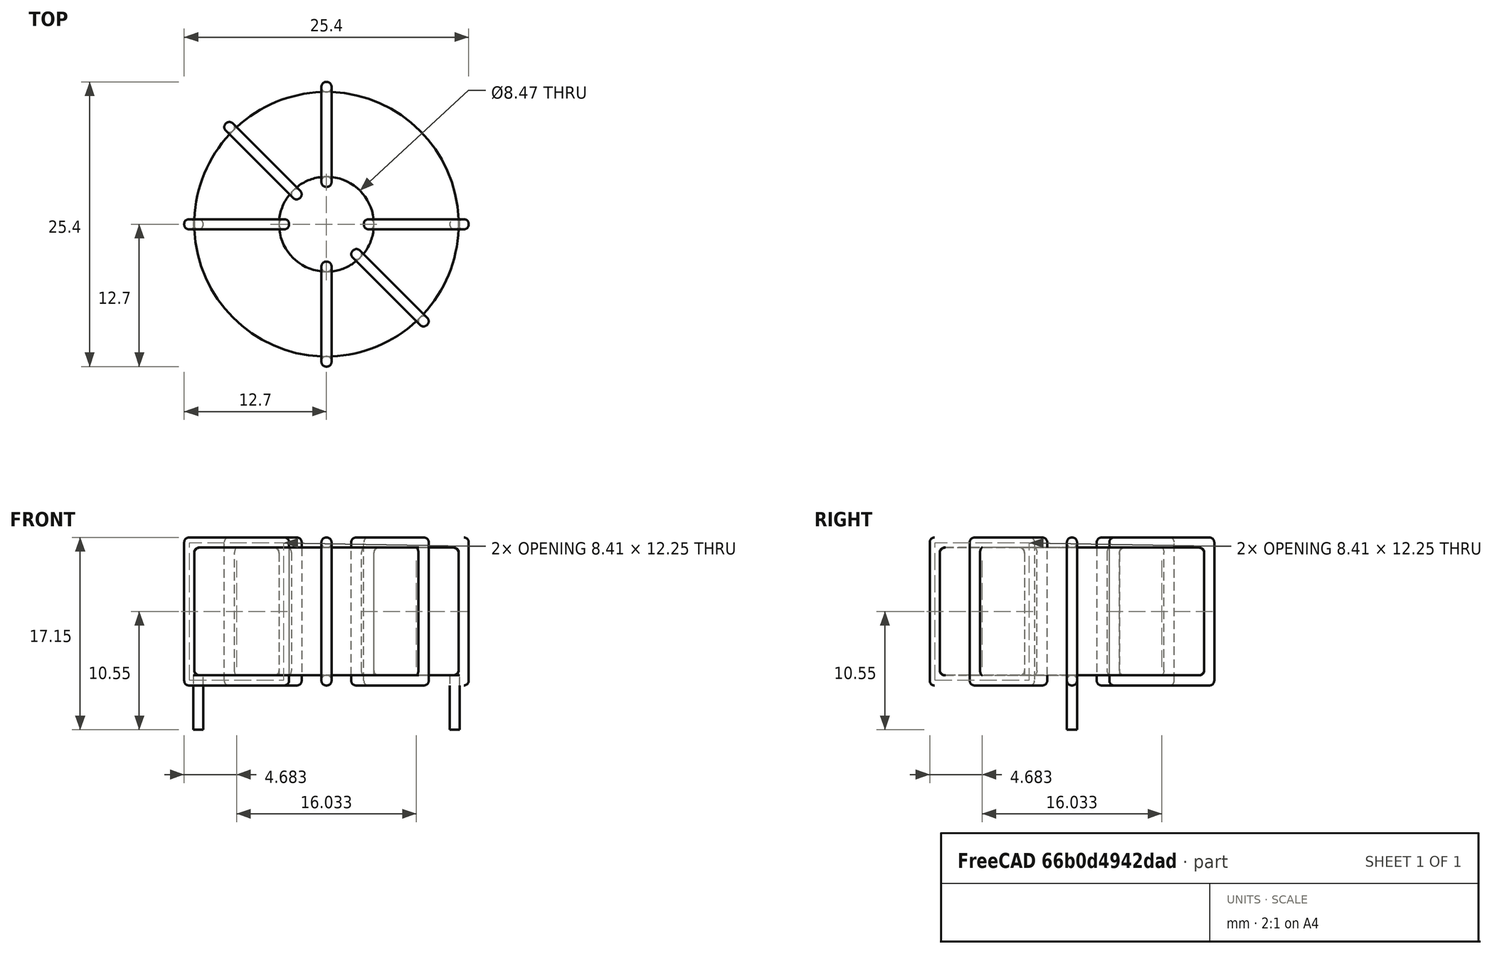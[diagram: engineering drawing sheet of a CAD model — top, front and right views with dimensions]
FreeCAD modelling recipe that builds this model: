
FCSTD DOCUMENT  (FreeCAD 0.16R6703 (Git))
Label: L_Toroid_Horizontal_D25.4mm_P22.90mm_Vishay_TJ5
License: All rights reserved
LicenseURL: http://en.wikipedia.org/wiki/All_rights_reserved
objects: Sketcher::SketchObject×6, PartDesign::Pad×6, PartDesign::Fillet×5, Spreadsheet::Sheet×1
note: 23 computed .brp shape members not serialized (recipe doc carries the construction recipe); baked Part::Feature solids carry a one-line shape summary decoded from their .brp

FEATURE [Spreadsheet::Sheet] Spreadsheet  label="dimensions"
  cells = A1=Wx; B1(Wx)=25.4; C1(WW)=8.466666666666667; D1=25.4; A2=Wy; B2(Wy)=25.4; D2=25.4; A3=RM; B3(RMx)=22.9; C3(RMy)=0; A4=d_wire; B4(d_wire)=0.8999999999999999; A5=H; B5(H)=11.4; A6=offsetx; B6(offsetx)=1.25
FEATURE [Sketcher::SketchObject] Sketch
  Placement = pos=(0,0,1.4) rot=(0,0,1;0rad)
  expr: Placement.Base.z = 0.5 + Spreadsheet.d_wire
  expr: Constraints[0] = Spreadsheet.Wx / 2 - Spreadsheet.d_wire
  expr: Constraints[4] = Spreadsheet.WW / 2
  expr: Constraints[2] = Spreadsheet.RMy / 2
  expr: Constraints[1] = Spreadsheet.RMx / 2
  sketch-geometry (2):
    g0: Circle CenterX=11.45 CenterY=0 CenterZ=0 NormalX=0 NormalY=0 NormalZ=1 Radius=11.8
    g1: Circle CenterX=11.45 CenterY=0 CenterZ=0 NormalX=0 NormalY=0 NormalZ=1 Radius=4.23333
  constraints (5):
    c: Radius(g0) = 11.8
    c: DistanceX(g-1,g0) = 11.45
    c: DistanceY(g-1,g0) = 0
    c: Coincident(g1,g0)
    c: Radius(g1) = 4.23333
FEATURE [PartDesign::Pad] Pad
  Length = 11.4
  Length2 = 100
  Placement = pos=(0,0,1.4) rot=(0,0,1;0rad)
  Sketch = -> Sketch
  Type = 0
  expr: Length = Spreadsheet.H
FEATURE [Sketcher::SketchObject] Sketch001
  Placement = pos=(0,0,0.95) rot=(0,0,1;0rad)
  expr: Placement.Base.z = 0.5 + Spreadsheet.d_wire * 0.5
  expr: Constraints[4] = Spreadsheet.RMx
  expr: Constraints[2] = Spreadsheet.RMy
  expr: Constraints[1] = Spreadsheet.d_wire / 2
  sketch-geometry (2):
    g0: Circle CenterX=0 CenterY=0 CenterZ=0 NormalX=0 NormalY=0 NormalZ=1 Radius=0.45
    g1: Circle CenterX=22.9 CenterY=0 CenterZ=0 NormalX=0 NormalY=0 NormalZ=1 Radius=0.45
  constraints (5):
    c: Equal(g0,g1)
    c: Radius(g0) = 0.45
    c: DistanceY(g-1,g1) = 0
    c: Coincident(g0,g-1)
    c: DistanceX(g-1,g1) = 22.9
FEATURE [PartDesign::Pad] Pad001
  Length = 0.45
  Length2 = 4.4
  Placement = pos=(0,0,0.95) rot=(0,0,1;0rad)
  Reversed = true
  Sketch = -> Sketch001
  Type = 4
  expr: Length2 = 3.5 + Spreadsheet.d_wire
  expr: Length = Spreadsheet.d_wire / 2
FEATURE [PartDesign::Fillet] Fillet
  Base = -> Pad [Edge6,Edge3,Edge2]
  Placement = pos=(0,0,1.4) rot=(0,0,1;0rad)
  Radius = 0.5
FEATURE [Sketcher::SketchObject] Sketch003
  Placement = pos=(11.45,0,0) rot=(1,0,0;1.5708rad)
  expr: Placement.Base.x = Spreadsheet.RMx / 2
  expr: Constraints[49] = Spreadsheet.Wx - Spreadsheet.d_wire * 2
  expr: Constraints[44] = Spreadsheet.d_wire
  expr: Constraints[23] = Spreadsheet.H
  expr: Constraints[22] = Spreadsheet.Wx / 2 - Spreadsheet.d_wire
  expr: Placement.Base.y = Spreadsheet.RMy / 2
  expr: Constraints[21] = (Spreadsheet.Wx - Spreadsheet.WW) / 2 - Spreadsheet.d_wire
  expr: Constraints[19] = Spreadsheet.d_wire
  expr: Constraints[17] = Spreadsheet.d_wire
  expr: Constraints[18] = Spreadsheet.d_wire
  expr: Constraints[16] = Spreadsheet.d_wire
  sketch-geometry (16):
    g0: LineSegment StartX=-3.33333 StartY=0.5 StartZ=0 EndX=-12.7 EndY=0.5 EndZ=0
    g1: LineSegment StartX=-12.7 StartY=0.5 StartZ=0 EndX=-12.7 EndY=13.7 EndZ=0
    g2: LineSegment StartX=-12.7 StartY=13.7 StartZ=0 EndX=-3.33333 EndY=13.7 EndZ=0
    g3: LineSegment StartX=-3.33333 StartY=13.7 StartZ=0 EndX=-3.33333 EndY=0.5 EndZ=0
    g4: LineSegment StartX=-11.8 StartY=12.8 StartZ=0 EndX=-4.23333 EndY=12.8 EndZ=0
    g5: LineSegment StartX=-4.23333 StartY=12.8 StartZ=0 EndX=-4.23333 EndY=1.4 EndZ=0
    g6: LineSegment StartX=-4.23333 StartY=1.4 StartZ=0 EndX=-11.8 EndY=1.4 EndZ=0
    g7: LineSegment StartX=-11.8 StartY=1.4 StartZ=0 EndX=-11.8 EndY=12.8 EndZ=0
    g8: LineSegment StartX=3.33333 StartY=13.7 StartZ=0 EndX=12.7 EndY=13.7 EndZ=0
    g9: LineSegment StartX=12.7 StartY=13.7 StartZ=0 EndX=12.7 EndY=0.5 EndZ=0
    g10: LineSegment StartX=12.7 StartY=0.5 StartZ=0 EndX=3.33333 EndY=0.5 EndZ=0
    g11: LineSegment StartX=3.33333 StartY=0.5 StartZ=0 EndX=3.33333 EndY=13.7 EndZ=0
    g12: LineSegment StartX=4.23333 StartY=12.8 StartZ=0 EndX=11.8 EndY=12.8 EndZ=0
    g13: LineSegment StartX=11.8 StartY=12.8 StartZ=0 EndX=11.8 EndY=1.4 EndZ=0
    g14: LineSegment StartX=11.8 StartY=1.4 StartZ=0 EndX=4.23333 EndY=1.4 EndZ=0
    g15: LineSegment StartX=4.23333 StartY=1.4 StartZ=0 EndX=4.23333 EndY=12.8 EndZ=0
  constraints (50):
    c: Horizontal(g0)
    c: Coincident(g1,g0)
    c: Vertical(g1)
    c: Coincident(g2,g1)
    c: Horizontal(g2)
    c: Coincident(g3,g2)
    c: Coincident(g3,g0)
    c: Vertical(g3)
    c: Coincident(g4,g5)
    c: Coincident(g5,g6)
    c: Coincident(g6,g7)
    c: Coincident(g7,g4)
    c: Horizontal(g4)
    c: Horizontal(g6)
    c: Vertical(g5)
    c: Vertical(g7)
    c: DistanceX(g1,g4) = 0.9
    c: DistanceY(g4,g1) = 0.9
    c: DistanceX(g5,g0) = 0.9
    c: DistanceY(g0,g5) = 0.9
    c: DistanceY(g-1,g0) = 0.5
    c: DistanceX(g6,g6) = 7.56667
    c: DistanceX(g6,g-1) = 11.8
    c: DistanceY(g7,g7) = 11.4
    c: Coincident(g8,g9)
    c: Coincident(g9,g10)
    c: Coincident(g10,g11)
    c: Coincident(g11,g8)
    c: Horizontal(g8)
    c: Horizontal(g10)
    c: Vertical(g9)
    c: Vertical(g11)
    c: Coincident(g12,g13)
    c: Coincident(g13,g14)
    c: Coincident(g14,g15)
    c: Coincident(g15,g12)
    c: Horizontal(g12)
    c: Horizontal(g14)
    c: Vertical(g13)
    c: Vertical(g15)
    c: DistanceY(g8,g2) = 0
    c: DistanceY(g10,g0) = 0
    c: DistanceY(g14,g5) = 0
    c: DistanceY(g12,g4) = 0
    c: DistanceX(g8,g12) = 0.9
    c: Equal(g8,g2)
    c: Equal(g12,g4)
    c: Equal(g9,g1)
    c: Equal(g13,g7)
    c: DistanceX(g4,g12) = 23.6
FEATURE [PartDesign::Pad] Pad002
  Length = 0.9
  Length2 = 100
  Midplane = true
  Placement = pos=(11.45,0,0) rot=(1,0,0;1.5708rad)
  Sketch = -> Sketch003
  Type = 0
  expr: Length = Spreadsheet.d_wire
FEATURE [PartDesign::Fillet] Fillet001
  Base = -> Pad002 [Edge38,Edge41,Edge42,Edge43,Edge29,Edge32,Edge33,Edge34,Edge25,Edge35,Edge36,Edge13,Edge14,Edge15,Edge16,Edge17,Edge18,Edge19,Edge1,Edge2,Edge3,Edge4,Edge5,Edge6,Edge7,Edge37,Edge39,Edge40,Edge20,Edge23,Edge24,Edge21,Edge22,Edge8,Edge9,Edge10,Edge11,Edge12,Edge26,Edge27,+8 more]
  Placement = pos=(11.45,0,0) rot=(1,0,0;1.5708rad)
  Radius = 0.423
  expr: Radius = Spreadsheet.d_wire * 0.47
FEATURE [Sketcher::SketchObject] Sketch004
  Placement = pos=(11.45,0,0) rot=(0.862856,0.357407,0.357407;1.71777rad)
  expr: Placement.Base.x = Spreadsheet.RMx / 2
  expr: Constraints[49] = Spreadsheet.Wx - 2 * Spreadsheet.d_wire
  expr: Constraints[44] = Spreadsheet.d_wire
  expr: Constraints[23] = Spreadsheet.H
  expr: Constraints[22] = Spreadsheet.Wx / 2 - Spreadsheet.d_wire
  expr: Placement.Base.y = Spreadsheet.RMy / 2
  expr: Constraints[21] = (Spreadsheet.Wx - Spreadsheet.WW) / 2 - Spreadsheet.d_wire
  expr: Constraints[19] = Spreadsheet.d_wire
  expr: Constraints[17] = Spreadsheet.d_wire
  expr: Constraints[18] = Spreadsheet.d_wire
  expr: Constraints[16] = Spreadsheet.d_wire
  sketch-geometry (16):
    g0: LineSegment StartX=-3.33333 StartY=0.5 StartZ=0 EndX=-12.7 EndY=0.5 EndZ=0
    g1: LineSegment StartX=-12.7 StartY=0.5 StartZ=0 EndX=-12.7 EndY=13.7 EndZ=0
    g2: LineSegment StartX=-12.7 StartY=13.7 StartZ=0 EndX=-3.33333 EndY=13.7 EndZ=0
    g3: LineSegment StartX=-3.33333 StartY=13.7 StartZ=0 EndX=-3.33333 EndY=0.5 EndZ=0
    g4: LineSegment StartX=-11.8 StartY=12.8 StartZ=0 EndX=-4.23333 EndY=12.8 EndZ=0
    g5: LineSegment StartX=-4.23333 StartY=12.8 StartZ=0 EndX=-4.23333 EndY=1.4 EndZ=0
    g6: LineSegment StartX=-4.23333 StartY=1.4 StartZ=0 EndX=-11.8 EndY=1.4 EndZ=0
    g7: LineSegment StartX=-11.8 StartY=1.4 StartZ=0 EndX=-11.8 EndY=12.8 EndZ=0
    g8: LineSegment StartX=3.33333 StartY=13.7 StartZ=0 EndX=12.7 EndY=13.7 EndZ=0
    g9: LineSegment StartX=12.7 StartY=13.7 StartZ=0 EndX=12.7 EndY=0.5 EndZ=0
    g10: LineSegment StartX=12.7 StartY=0.5 StartZ=0 EndX=3.33333 EndY=0.5 EndZ=0
    g11: LineSegment StartX=3.33333 StartY=0.5 StartZ=0 EndX=3.33333 EndY=13.7 EndZ=0
    g12: LineSegment StartX=4.23333 StartY=12.8 StartZ=0 EndX=11.8 EndY=12.8 EndZ=0
    g13: LineSegment StartX=11.8 StartY=12.8 StartZ=0 EndX=11.8 EndY=1.4 EndZ=0
    g14: LineSegment StartX=11.8 StartY=1.4 StartZ=0 EndX=4.23333 EndY=1.4 EndZ=0
    g15: LineSegment StartX=4.23333 StartY=1.4 StartZ=0 EndX=4.23333 EndY=12.8 EndZ=0
  constraints (50):
    c: Horizontal(g0)
    c: Coincident(g1,g0)
    c: Vertical(g1)
    c: Coincident(g2,g1)
    c: Horizontal(g2)
    c: Coincident(g3,g2)
    c: Coincident(g3,g0)
    c: Vertical(g3)
    c: Coincident(g4,g5)
    c: Coincident(g5,g6)
    c: Coincident(g6,g7)
    c: Coincident(g7,g4)
    c: Horizontal(g4)
    c: Horizontal(g6)
    c: Vertical(g5)
    c: Vertical(g7)
    c: DistanceX(g1,g4) = 0.9
    c: DistanceY(g4,g1) = 0.9
    c: DistanceX(g5,g0) = 0.9
    c: DistanceY(g0,g5) = 0.9
    c: DistanceY(g-1,g0) = 0.5
    c: DistanceX(g6,g6) = 7.56667
    c: DistanceX(g6,g-1) = 11.8
    c: DistanceY(g7,g7) = 11.4
    c: Coincident(g8,g9)
    c: Coincident(g9,g10)
    c: Coincident(g10,g11)
    c: Coincident(g11,g8)
    c: Horizontal(g8)
    c: Horizontal(g10)
    c: Vertical(g9)
    c: Vertical(g11)
    c: Coincident(g12,g13)
    c: Coincident(g13,g14)
    c: Coincident(g14,g15)
    c: Coincident(g15,g12)
    c: Horizontal(g12)
    c: Horizontal(g14)
    c: Vertical(g13)
    c: Vertical(g15)
    c: DistanceY(g8,g2) = 0
    c: DistanceY(g10,g0) = 0
    c: DistanceY(g14,g5) = 0
    c: DistanceY(g12,g4) = 0
    c: DistanceX(g8,g12) = 0.9
    c: Equal(g8,g2)
    c: Equal(g12,g4)
    c: Equal(g9,g1)
    c: Equal(g13,g7)
    c: DistanceX(g4,g12) = 23.6
FEATURE [PartDesign::Pad] Pad003
  Length = 0.9
  Length2 = 100
  Midplane = true
  Placement = pos=(11.45,0,0) rot=(0.862856,0.357407,0.357407;1.71777rad)
  Sketch = -> Sketch004
  Type = 0
  expr: Length = Spreadsheet.d_wire
FEATURE [PartDesign::Fillet] Fillet002
  Base = -> Pad003 [Edge38,Edge41,Edge42,Edge43,Edge29,Edge32,Edge33,Edge34,Edge25,Edge35,Edge36,Edge13,Edge14,Edge15,Edge16,Edge17,Edge18,Edge19,Edge1,Edge2,Edge3,Edge4,Edge5,Edge6,Edge7,Edge37,Edge39,Edge40,Edge20,Edge23,Edge24,Edge21,Edge22,Edge8,Edge9,Edge10,Edge11,Edge12,Edge26,Edge27,+8 more]
  Placement = pos=(11.45,0,0) rot=(0.862856,0.357407,0.357407;1.71777rad)
  Radius = 0.423
  expr: Radius = Spreadsheet.d_wire * 0.47
FEATURE [Sketcher::SketchObject] Sketch005
  Placement = pos=(11.45,0,0) rot=(0.862856,-0.357407,-0.357407;1.71777rad)
  expr: Placement.Base.x = Spreadsheet.RMx / 2
  expr: Constraints[49] = Spreadsheet.Wx - 2 * Spreadsheet.d_wire
  expr: Constraints[44] = Spreadsheet.d_wire
  expr: Constraints[23] = Spreadsheet.H
  expr: Constraints[22] = Spreadsheet.Wx / 2 - Spreadsheet.d_wire
  expr: Placement.Base.y = Spreadsheet.RMy / 2
  expr: Constraints[21] = (Spreadsheet.Wx - Spreadsheet.WW) / 2 - Spreadsheet.d_wire
  expr: Constraints[19] = Spreadsheet.d_wire
  expr: Constraints[17] = Spreadsheet.d_wire
  expr: Constraints[18] = Spreadsheet.d_wire
  expr: Constraints[16] = Spreadsheet.d_wire
  sketch-geometry (16):
    g0: LineSegment StartX=-3.33333 StartY=0.5 StartZ=0 EndX=-12.7 EndY=0.5 EndZ=0
    g1: LineSegment StartX=-12.7 StartY=0.5 StartZ=0 EndX=-12.7 EndY=13.7 EndZ=0
    g2: LineSegment StartX=-12.7 StartY=13.7 StartZ=0 EndX=-3.33333 EndY=13.7 EndZ=0
    g3: LineSegment StartX=-3.33333 StartY=13.7 StartZ=0 EndX=-3.33333 EndY=0.5 EndZ=0
    g4: LineSegment StartX=-11.8 StartY=12.8 StartZ=0 EndX=-4.23333 EndY=12.8 EndZ=0
    g5: LineSegment StartX=-4.23333 StartY=12.8 StartZ=0 EndX=-4.23333 EndY=1.4 EndZ=0
    g6: LineSegment StartX=-4.23333 StartY=1.4 StartZ=0 EndX=-11.8 EndY=1.4 EndZ=0
    g7: LineSegment StartX=-11.8 StartY=1.4 StartZ=0 EndX=-11.8 EndY=12.8 EndZ=0
    g8: LineSegment StartX=3.33333 StartY=13.7 StartZ=0 EndX=12.7 EndY=13.7 EndZ=0
    g9: LineSegment StartX=12.7 StartY=13.7 StartZ=0 EndX=12.7 EndY=0.5 EndZ=0
    g10: LineSegment StartX=12.7 StartY=0.5 StartZ=0 EndX=3.33333 EndY=0.5 EndZ=0
    g11: LineSegment StartX=3.33333 StartY=0.5 StartZ=0 EndX=3.33333 EndY=13.7 EndZ=0
    g12: LineSegment StartX=4.23333 StartY=12.8 StartZ=0 EndX=11.8 EndY=12.8 EndZ=0
    g13: LineSegment StartX=11.8 StartY=12.8 StartZ=0 EndX=11.8 EndY=1.4 EndZ=0
    g14: LineSegment StartX=11.8 StartY=1.4 StartZ=0 EndX=4.23333 EndY=1.4 EndZ=0
    g15: LineSegment StartX=4.23333 StartY=1.4 StartZ=0 EndX=4.23333 EndY=12.8 EndZ=0
  constraints (50):
    c: Horizontal(g0)
    c: Coincident(g1,g0)
    c: Vertical(g1)
    c: Coincident(g2,g1)
    c: Horizontal(g2)
    c: Coincident(g3,g2)
    c: Coincident(g3,g0)
    c: Vertical(g3)
    c: Coincident(g4,g5)
    c: Coincident(g5,g6)
    c: Coincident(g6,g7)
    c: Coincident(g7,g4)
    c: Horizontal(g4)
    c: Horizontal(g6)
    c: Vertical(g5)
    c: Vertical(g7)
    c: DistanceX(g1,g4) = 0.9
    c: DistanceY(g4,g1) = 0.9
    c: DistanceX(g5,g0) = 0.9
    c: DistanceY(g0,g5) = 0.9
    c: DistanceY(g-1,g0) = 0.5
    c: DistanceX(g6,g6) = 7.56667
    c: DistanceX(g6,g-1) = 11.8
    c: DistanceY(g7,g7) = 11.4
    c: Coincident(g8,g9)
    c: Coincident(g9,g10)
    c: Coincident(g10,g11)
    c: Coincident(g11,g8)
    c: Horizontal(g8)
    c: Horizontal(g10)
    c: Vertical(g9)
    c: Vertical(g11)
    c: Coincident(g12,g13)
    c: Coincident(g13,g14)
    c: Coincident(g14,g15)
    c: Coincident(g15,g12)
    c: Horizontal(g12)
    c: Horizontal(g14)
    c: Vertical(g13)
    c: Vertical(g15)
    c: DistanceY(g8,g2) = 0
    c: DistanceY(g10,g0) = 0
    c: DistanceY(g14,g5) = 0
    c: DistanceY(g12,g4) = 0
    c: DistanceX(g8,g12) = 0.9
    c: Equal(g8,g2)
    c: Equal(g12,g4)
    c: Equal(g9,g1)
    c: Equal(g13,g7)
    c: DistanceX(g4,g12) = 23.6
FEATURE [PartDesign::Pad] Pad004
  Length = 0.9
  Length2 = 100
  Midplane = true
  Placement = pos=(11.45,0,0) rot=(0.862856,-0.357407,-0.357407;1.71777rad)
  Sketch = -> Sketch005
  Type = 0
  expr: Length = Spreadsheet.d_wire
FEATURE [PartDesign::Fillet] Fillet003
  Base = -> Pad004 [Edge38,Edge41,Edge42,Edge43,Edge29,Edge32,Edge33,Edge34,Edge25,Edge35,Edge36,Edge13,Edge14,Edge15,Edge16,Edge17,Edge18,Edge19,Edge1,Edge2,Edge3,Edge4,Edge5,Edge6,Edge7,Edge37,Edge39,Edge40,Edge20,Edge23,Edge24,Edge21,Edge22,Edge8,Edge9,Edge10,Edge11,Edge12,Edge26,Edge27,+8 more]
  Placement = pos=(11.45,0,0) rot=(0.862856,-0.357407,-0.357407;1.71777rad)
  Radius = 0.423
  expr: Radius = Spreadsheet.d_wire * 0.47
FEATURE [Sketcher::SketchObject] Sketch006
  Placement = pos=(11.45,0,0) rot=(0.57735,0.57735,0.57735;2.0944rad)
  expr: Placement.Base.x = Spreadsheet.RMx / 2
  expr: Constraints[49] = Spreadsheet.Wx - Spreadsheet.d_wire * 2
  expr: Constraints[44] = Spreadsheet.d_wire
  expr: Constraints[23] = Spreadsheet.H
  expr: Constraints[22] = Spreadsheet.Wx / 2 - Spreadsheet.d_wire
  expr: Placement.Base.y = Spreadsheet.RMy / 2
  expr: Constraints[21] = (Spreadsheet.Wx - Spreadsheet.WW) / 2 - Spreadsheet.d_wire
  expr: Constraints[19] = Spreadsheet.d_wire
  expr: Constraints[17] = Spreadsheet.d_wire
  expr: Constraints[18] = Spreadsheet.d_wire
  expr: Constraints[16] = Spreadsheet.d_wire
  sketch-geometry (16):
    g0: LineSegment StartX=-3.33333 StartY=0.5 StartZ=0 EndX=-12.7 EndY=0.5 EndZ=0
    g1: LineSegment StartX=-12.7 StartY=0.5 StartZ=0 EndX=-12.7 EndY=13.7 EndZ=0
    g2: LineSegment StartX=-12.7 StartY=13.7 StartZ=0 EndX=-3.33333 EndY=13.7 EndZ=0
    g3: LineSegment StartX=-3.33333 StartY=13.7 StartZ=0 EndX=-3.33333 EndY=0.5 EndZ=0
    g4: LineSegment StartX=-11.8 StartY=12.8 StartZ=0 EndX=-4.23333 EndY=12.8 EndZ=0
    g5: LineSegment StartX=-4.23333 StartY=12.8 StartZ=0 EndX=-4.23333 EndY=1.4 EndZ=0
    g6: LineSegment StartX=-4.23333 StartY=1.4 StartZ=0 EndX=-11.8 EndY=1.4 EndZ=0
    g7: LineSegment StartX=-11.8 StartY=1.4 StartZ=0 EndX=-11.8 EndY=12.8 EndZ=0
    g8: LineSegment StartX=3.33333 StartY=13.7 StartZ=0 EndX=12.7 EndY=13.7 EndZ=0
    g9: LineSegment StartX=12.7 StartY=13.7 StartZ=0 EndX=12.7 EndY=0.5 EndZ=0
    g10: LineSegment StartX=12.7 StartY=0.5 StartZ=0 EndX=3.33333 EndY=0.5 EndZ=0
    g11: LineSegment StartX=3.33333 StartY=0.5 StartZ=0 EndX=3.33333 EndY=13.7 EndZ=0
    g12: LineSegment StartX=4.23333 StartY=12.8 StartZ=0 EndX=11.8 EndY=12.8 EndZ=0
    g13: LineSegment StartX=11.8 StartY=12.8 StartZ=0 EndX=11.8 EndY=1.4 EndZ=0
    g14: LineSegment StartX=11.8 StartY=1.4 StartZ=0 EndX=4.23333 EndY=1.4 EndZ=0
    g15: LineSegment StartX=4.23333 StartY=1.4 StartZ=0 EndX=4.23333 EndY=12.8 EndZ=0
  constraints (50):
    c: Horizontal(g0)
    c: Coincident(g1,g0)
    c: Vertical(g1)
    c: Coincident(g2,g1)
    c: Horizontal(g2)
    c: Coincident(g3,g2)
    c: Coincident(g3,g0)
    c: Vertical(g3)
    c: Coincident(g4,g5)
    c: Coincident(g5,g6)
    c: Coincident(g6,g7)
    c: Coincident(g7,g4)
    c: Horizontal(g4)
    c: Horizontal(g6)
    c: Vertical(g5)
    c: Vertical(g7)
    c: DistanceX(g1,g4) = 0.9
    c: DistanceY(g4,g1) = 0.9
    c: DistanceX(g5,g0) = 0.9
    c: DistanceY(g0,g5) = 0.9
    c: DistanceY(g-1,g0) = 0.5
    c: DistanceX(g6,g6) = 7.56667
    c: DistanceX(g6,g-1) = 11.8
    c: DistanceY(g7,g7) = 11.4
    c: Coincident(g8,g9)
    c: Coincident(g9,g10)
    c: Coincident(g10,g11)
    c: Coincident(g11,g8)
    c: Horizontal(g8)
    c: Horizontal(g10)
    c: Vertical(g9)
    c: Vertical(g11)
    c: Coincident(g12,g13)
    c: Coincident(g13,g14)
    c: Coincident(g14,g15)
    c: Coincident(g15,g12)
    c: Horizontal(g12)
    c: Horizontal(g14)
    c: Vertical(g13)
    c: Vertical(g15)
    c: DistanceY(g8,g2) = 0
    c: DistanceY(g10,g0) = 0
    c: DistanceY(g14,g5) = 0
    c: DistanceY(g12,g4) = 0
    c: DistanceX(g8,g12) = 0.9
    c: Equal(g8,g2)
    c: Equal(g12,g4)
    c: Equal(g9,g1)
    c: Equal(g13,g7)
    c: DistanceX(g4,g12) = 23.6
FEATURE [PartDesign::Pad] Pad005
  Length = 0.9
  Length2 = 100
  Midplane = true
  Placement = pos=(11.45,0,0) rot=(0.57735,0.57735,0.57735;2.0944rad)
  Sketch = -> Sketch006
  Type = 0
  expr: Length = Spreadsheet.d_wire
FEATURE [PartDesign::Fillet] Fillet004
  Base = -> Pad005 [Edge38,Edge41,Edge42,Edge43,Edge29,Edge32,Edge33,Edge34,Edge25,Edge35,Edge36,Edge13,Edge14,Edge15,Edge16,Edge17,Edge18,Edge19,Edge1,Edge2,Edge3,Edge4,Edge5,Edge6,Edge7,Edge37,Edge39,Edge40,Edge20,Edge23,Edge24,Edge21,Edge22,Edge8,Edge9,Edge10,Edge11,Edge12,Edge26,Edge27,+8 more]
  Placement = pos=(11.45,0,0) rot=(0.57735,0.57735,0.57735;2.0944rad)
  Radius = 0.423
  expr: Radius = Spreadsheet.d_wire * 0.47
